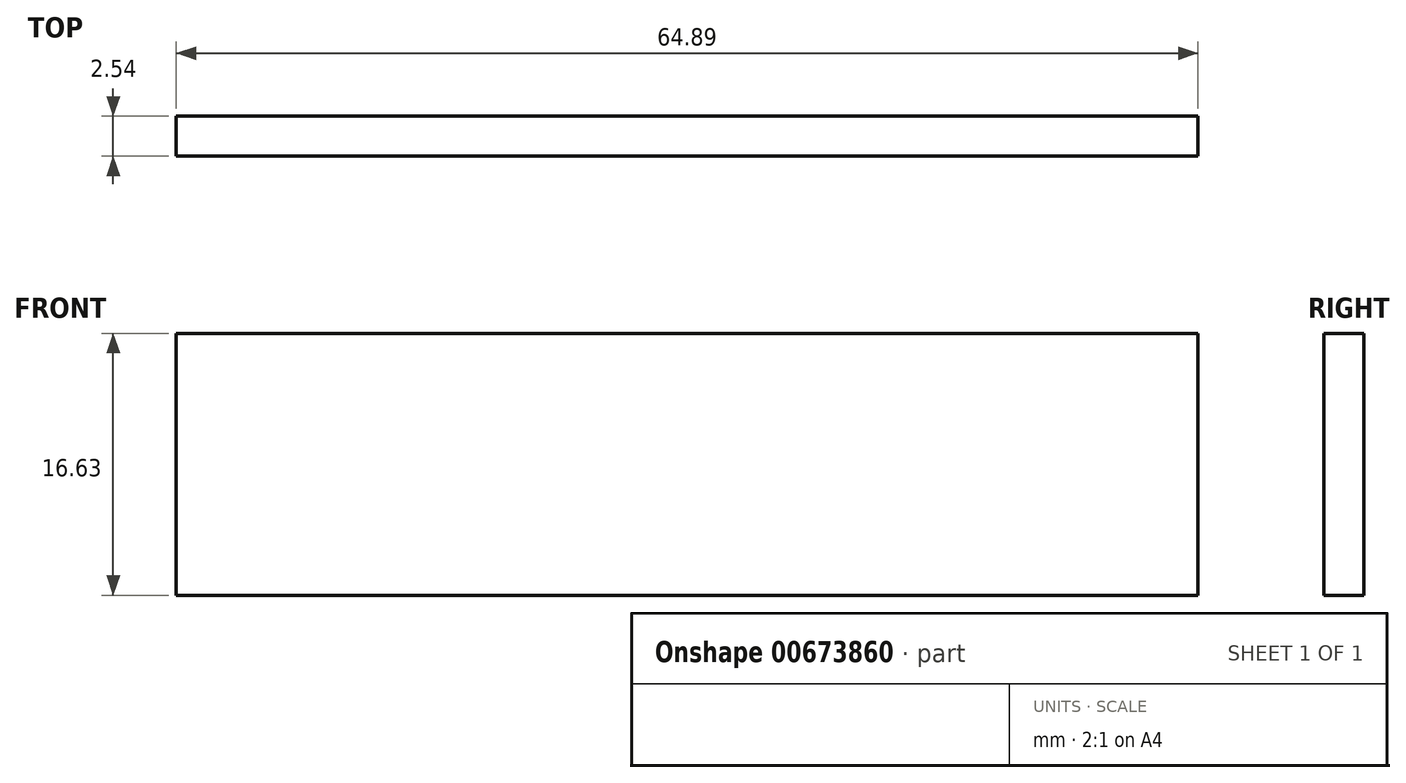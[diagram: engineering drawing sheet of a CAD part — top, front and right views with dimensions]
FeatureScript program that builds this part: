
annotation { "Feature Type Name" : "Feature", "Feature Type Description" : "" }
export const myFeature = defineFeature(function(context is Context, id is Id, definition is map)
    precondition{}
    {
        {
            var Q0;
            Q0=qCreatedBy(makeId("Front.planeOp"),FACE);
            var sketch = newSketch(context, id + "F0", { "sketchPlane" : qUnion([Q0])});
            skLineSegment(sketch, "E0.bottom", {"start": v(0, 0) * mm, "end": v(64.9, 0) * mm});
            skLineSegment(sketch, "E0.top", {"start": v(0, 16.63) * mm, "end": v(64.9, 16.63) * mm});
            skLineSegment(sketch, "E0.left", {"start": v(0, 0) * mm, "end": v(0, 16.63) * mm});
            skLineSegment(sketch, "E0.right", {"start": v(64.9, 0) * mm, "end": v(64.9, 16.63) * mm});
            skSolve(sketch);
        }
        {
            var Q0;
            Q0=makeQuery(id+"F0.imprint","IMPRINT",FACE,{"disambiguationData":[TD([[makeQuery(id+"F0.imprint","IMPRINT",EDGE,{"derivedFrom":sQuery(id+"F0.wireOp",EDGE,"E0.bottom")}),1.0]])]});
            extrude(context, id + "F1", {"entities" : qUnion([Q0]), "depth" : 2.54 * mm, "offsetDistance" : 25.4 * mm});
        }
    });
